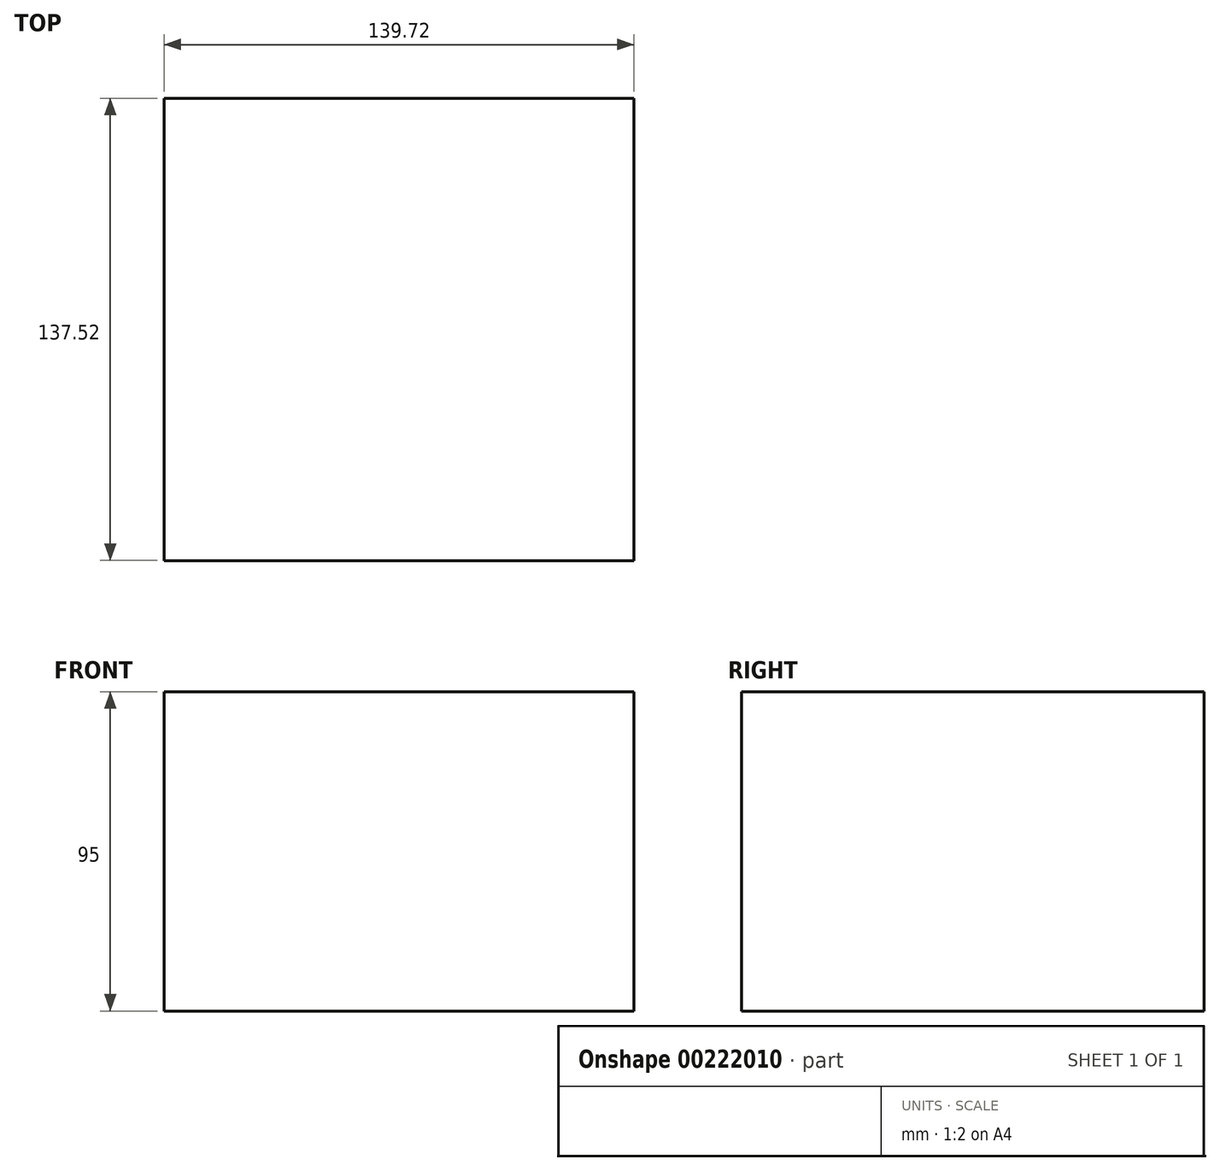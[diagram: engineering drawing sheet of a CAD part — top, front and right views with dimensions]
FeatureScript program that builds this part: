
annotation { "Feature Type Name" : "Feature", "Feature Type Description" : "" }
export const myFeature = defineFeature(function(context is Context, id is Id, definition is map)
    precondition{}
    {
        {
            var Q0;
            Q0=qCreatedBy(makeId("Top.planeOp"),FACE);
            var sketch = newSketch(context, id + "F0", { "sketchPlane" : qUnion([Q0])});
            skLineSegment(sketch, "E0.bottom", {"start": v(69.86, -68.76) * mm, "end": v(-69.86, -68.76) * mm});
            skLineSegment(sketch, "E0.top", {"start": v(69.86, 68.76) * mm, "end": v(-69.86, 68.76) * mm});
            skLineSegment(sketch, "E0.left", {"start": v(69.86, -68.76) * mm, "end": v(69.86, 68.76) * mm});
            skLineSegment(sketch, "E0.right", {"start": v(-69.86, -68.76) * mm, "end": v(-69.86, 68.76) * mm});
            skPoint(sketch, "E0.middle", {"position": v(0, 0) * mm});
            skLineSegment(sketch, "E1", {"start": v(0, 68.76) * mm, "end": v(0, -68.76) * mm});
            skSolve(sketch);
        }
        {
            var Q0;
            Q0=qCreatedBy(makeId("Top.planeOp"),FACE);
            var sketch = newSketch(context, id + "F1", { "sketchPlane" : qUnion([Q0])});
            skCircle(sketch, "E2", {"center": v(54.26, 0) * mm, "radius": 9.82 * mm});
            skSolve(sketch);
        }
        {
            var Q0;
            Q0=sQuery(id+"F1.wireOp",EDGE,"E2");
            var Q1;
            Q1=sQuery(id+"F0.wireOp",EDGE,"E1");
            revolve(context, id + "F2", {"bodyType" : ToolBodyType.SURFACE, "surfaceEntities" : qUnion([Q0]), "axis" : qUnion([Q1]), "revolveType" : RevolveType.ONE_DIRECTION, "angle" : 182.43 * degree});
        }
        {
            var Q0;
            {var subQ0=sQuery(id+"F0.wireOp",EDGE,"E0.right");Q0=makeQuery(id+"F0.imprint","IMPRINT",FACE,{"disambiguationData":[TD([[makeQuery(id+"F0.imprint","IMPRINT",EDGE,{"derivedFrom":subQ0}),-1.0]])]});}
            var Q1;
            {var subQ0=sQuery(id+"F0.wireOp",EDGE,"E0.left");Q1=makeQuery(id+"F0.imprint","IMPRINT",FACE,{"disambiguationData":[TD([[makeQuery(id+"F0.imprint","IMPRINT",EDGE,{"derivedFrom":subQ0}),1.0]])]});}
            extrude(context, id + "F3", {"entities" : qUnion([Q0, Q1]), "oppositeDirection" : true, "depth" : 95 * mm});
        }
    });
